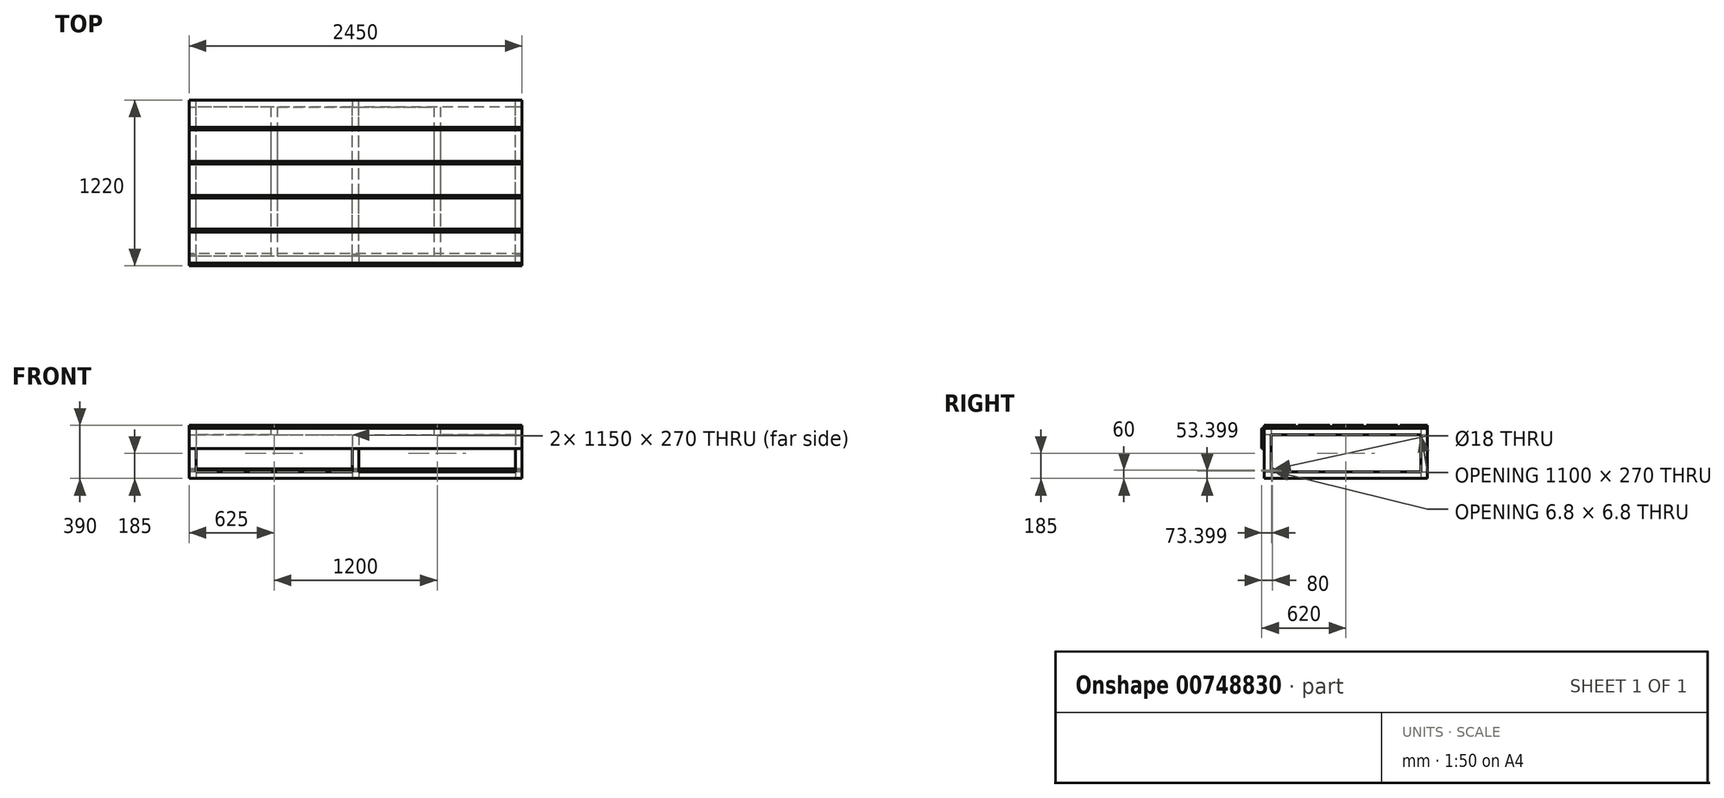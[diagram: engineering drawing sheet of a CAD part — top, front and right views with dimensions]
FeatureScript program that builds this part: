
annotation { "Feature Type Name" : "Feature", "Feature Type Description" : "" }
export const myFeature = defineFeature(function(context is Context, id is Id, definition is map)
    precondition{}
    {
        {
            var Q0;
            Q0=qCreatedBy(makeId("Top.planeOp"),FACE);
            var sketch = newSketch(context, id + "F0", { "sketchPlane" : qUnion([Q0])});
            skLineSegment(sketch, "E0.bottom", {"start": v(1225, -600) * mm, "end": v(-1225, -600) * mm});
            skLineSegment(sketch, "E0.top", {"start": v(1225, 600) * mm, "end": v(-1225, 600) * mm});
            skLineSegment(sketch, "E0.left", {"start": v(1225, -600) * mm, "end": v(1225, 600) * mm});
            skLineSegment(sketch, "E0.right", {"start": v(-1225, -600) * mm, "end": v(-1225, 600) * mm});
            skPoint(sketch, "E0.middle", {"position": v(0, 0) * mm});
            skLineSegment(sketch, "E1.0", {"start": v(1225, 550) * mm, "end": v(-1225, 550) * mm});
            skLineSegment(sketch, "E2.0", {"start": v(1227.5, -600) * mm, "end": v(1227.5, 600) * mm});
            skLineSegment(sketch, "E3.0", {"start": v(1175, -600) * mm, "end": v(1175, 600) * mm});
            skLineSegment(sketch, "E4.0", {"start": v(1225, -550) * mm, "end": v(-1225, -550) * mm});
            skLineSegment(sketch, "E5.0", {"start": v(-1175, -600) * mm, "end": v(-1175, 600) * mm});
            skLineSegment(sketch, "E6", {"start": v(0, 0) * mm, "end": v(0, 550) * mm});
            skLineSegment(sketch, "E7", {"start": v(0, 0) * mm, "end": v(0, -550) * mm});
            skLineSegment(sketch, "E8.0", {"start": v(25, 0) * mm, "end": v(25, 550) * mm});
            skLineSegment(sketch, "E9.0", {"start": v(-25, 0) * mm, "end": v(-25, 550) * mm});
            skLineSegment(sketch, "E10.0", {"start": v(-25, 0) * mm, "end": v(-25, -550) * mm});
            skLineSegment(sketch, "E11.0", {"start": v(25, 0) * mm, "end": v(25, -550) * mm});
            skSolve(sketch);
        }
        {
            var Q0;
            Q0=qSketchRegion(id+"F0",true);
            var Q1;
            {var subQ1=sQuery(id+"F0.wireOp",EDGE,"E6");Q1=makeQuery(id+"F0.imprint","IMPRINT",FACE,{"disambiguationData":[TD([[makeQuery(id+"F0.imprint","IMPRINT",EDGE,{"derivedFrom":subQ1}),-1.0]])]});}
            var Q2;
            {var subQ3=sQuery(id+"F0.wireOp",EDGE,"E6");Q2=makeQuery(id+"F0.imprint","IMPRINT",FACE,{"disambiguationData":[TD([[makeQuery(id+"F0.imprint","IMPRINT",EDGE,{"derivedFrom":subQ3}),1.0]])]});}
            extrude(context, id + "F1", {"entities" : qUnion([Q0, Q1, Q2]), "depth" : 50 * mm, "offsetDistance" : 25 * mm});
        }
        {
            var Q0;
            Q0=makeQuery(id+"F1.opExtrude","CAP_FACE",FACE,{"disambiguationData":[OSD([sQuery(id+"F0.wireOp",EDGE,"E0.bottom"),sQuery(id+"F0.wireOp",EDGE,"E0.top"),sQuery(id+"F0.wireOp",EDGE,"E0.left"),sQuery(id+"F0.wireOp",EDGE,"E0.right"),sQuery(id+"F0.wireOp",EDGE,"E1.0"),sQuery(id+"F0.wireOp",EDGE,"E3.0"),sQuery(id+"F0.wireOp",EDGE,"E4.0"),sQuery(id+"F0.wireOp",EDGE,"E5.0"),sQuery(id+"F0.wireOp",EDGE,"E8.0"),sQuery(id+"F0.wireOp",EDGE,"E9.0"),sQuery(id+"F0.wireOp",EDGE,"E10.0"),sQuery(id+"F0.wireOp",EDGE,"E11.0")])],"isStart":false});
            var sketch = newSketch(context, id + "F2", { "sketchPlane" : qUnion([Q0])});
            skLineSegment(sketch, "E12", {"start": v(-25, 550) * mm, "end": v(25, 550) * mm});
            skLineSegment(sketch, "E13", {"start": v(25, 550) * mm, "end": v(25, 600) * mm});
            skLineSegment(sketch, "E14", {"start": v(25, 600) * mm, "end": v(-25, 600) * mm});
            skLineSegment(sketch, "E15", {"start": v(-25, 600) * mm, "end": v(-25, 550) * mm});
            skLineSegment(sketch, "E16", {"start": v(-1175, 550) * mm, "end": v(-1175, 600) * mm});
            skLineSegment(sketch, "E17", {"start": v(-1175, 600) * mm, "end": v(-1225, 600) * mm});
            skLineSegment(sketch, "E18", {"start": v(-1225, 600) * mm, "end": v(-1225, 550) * mm});
            skLineSegment(sketch, "E19", {"start": v(-1225, 550) * mm, "end": v(-1175, 550) * mm});
            skLineSegment(sketch, "E20", {"start": v(-1175, -550) * mm, "end": v(-1175, -600) * mm});
            skLineSegment(sketch, "E21", {"start": v(-1175, -600) * mm, "end": v(-1225, -600) * mm});
            skLineSegment(sketch, "E22", {"start": v(-1225, -600) * mm, "end": v(-1225, -550) * mm});
            skLineSegment(sketch, "E23", {"start": v(-1225, -550) * mm, "end": v(-1175, -550) * mm});
            skLineSegment(sketch, "E24", {"start": v(-25, -550) * mm, "end": v(25, -550) * mm});
            skLineSegment(sketch, "E25", {"start": v(25, -550) * mm, "end": v(25, -600) * mm});
            skLineSegment(sketch, "E26", {"start": v(25, -600) * mm, "end": v(-25, -600) * mm});
            skPoint(sketch, "E26.endSnap0", {"position": v(0, -600) * mm});
            skLineSegment(sketch, "E27", {"start": v(-25, -600) * mm, "end": v(-25, -550) * mm});
            skLineSegment(sketch, "E28", {"start": v(1175, -550) * mm, "end": v(1225, -550) * mm});
            skLineSegment(sketch, "E29", {"start": v(1225, -550) * mm, "end": v(1225, -600) * mm});
            skLineSegment(sketch, "E30", {"start": v(1225, -600) * mm, "end": v(1175, -600) * mm});
            skLineSegment(sketch, "E31", {"start": v(1175, -600) * mm, "end": v(1175, -550) * mm});
            skLineSegment(sketch, "E32", {"start": v(1175, 550) * mm, "end": v(1175, 600) * mm});
            skLineSegment(sketch, "E33", {"start": v(1175, 600) * mm, "end": v(1225, 600) * mm});
            skLineSegment(sketch, "E34", {"start": v(1225, 600) * mm, "end": v(1225, 550) * mm});
            skLineSegment(sketch, "E35", {"start": v(1225, 550) * mm, "end": v(1175, 550) * mm});
            skSolve(sketch);
        }
        {
            var Q0;
            Q0=qSketchRegion(id+"F2",true);
            extrude(context, id + "F3", {"entities" : qUnion([Q0]), "operationType" : NewBodyOperationType.ADD, "depth" : 270 * mm, "offsetDistance" : 25 * mm});
        }
        {
            var Q0;
            Q0=makeQuery(id+"F3.opExtrude","CAP_FACE",FACE,{"disambiguationData":[OSD([sQuery(id+"F2.wireOp",EDGE,"E12"),sQuery(id+"F2.wireOp",EDGE,"E13"),sQuery(id+"F2.wireOp",EDGE,"E14"),sQuery(id+"F2.wireOp",EDGE,"E15")])],"isStart":false});
            var sketch = newSketch(context, id + "F4", { "sketchPlane" : qUnion([Q0])});
            skLineSegment(sketch, "E36.bottom", {"start": v(-1225, 600) * mm, "end": v(1225, 600) * mm});
            skLineSegment(sketch, "E36.top", {"start": v(-1225, -600) * mm, "end": v(1225, -600) * mm});
            skLineSegment(sketch, "E36.left", {"start": v(-1225, 600) * mm, "end": v(-1225, -600) * mm});
            skLineSegment(sketch, "E36.right", {"start": v(1225, 600) * mm, "end": v(1225, -600) * mm});
            skLineSegment(sketch, "E37.bottom", {"start": v(1175, -550) * mm, "end": v(-1175, -550) * mm});
            skLineSegment(sketch, "E37.top", {"start": v(1175, 550) * mm, "end": v(-1175, 550) * mm});
            skLineSegment(sketch, "E37.left", {"start": v(1175, -550) * mm, "end": v(1175, 550) * mm});
            skLineSegment(sketch, "E37.right", {"start": v(-1175, -550) * mm, "end": v(-1175, 550) * mm});
            skLineSegment(sketch, "E38.bottom", {"start": v(-25, 550) * mm, "end": v(25, 550) * mm});
            skLineSegment(sketch, "E38.top", {"start": v(-25, -550) * mm, "end": v(25, -550) * mm});
            skLineSegment(sketch, "E38.left", {"start": v(-25, 550) * mm, "end": v(-25, -550) * mm});
            skLineSegment(sketch, "E38.right", {"start": v(25, 550) * mm, "end": v(25, -550) * mm});
            skLineSegment(sketch, "E39", {"start": v(-25, 550) * mm, "end": v(-1175, 550) * mm});
            skLineSegment(sketch, "E40", {"start": v(-600, 550) * mm, "end": v(-600, -550) * mm});
            skLineSegment(sketch, "E41.0", {"start": v(-625, 550) * mm, "end": v(-625, -550) * mm});
            skLineSegment(sketch, "E42.0", {"start": v(-575, 550) * mm, "end": v(-575, -550) * mm});
            skLineSegment(sketch, "E43", {"start": v(25, 550) * mm, "end": v(1175, 550) * mm});
            skLineSegment(sketch, "E44", {"start": v(600, 550) * mm, "end": v(600, -550) * mm});
            skLineSegment(sketch, "E45.0", {"start": v(575, 550) * mm, "end": v(575, -550) * mm});
            skLineSegment(sketch, "E46.0", {"start": v(625, 550) * mm, "end": v(625, -550) * mm});
            skSolve(sketch);
        }
        {
            var Q0;
            Q0=qSketchRegion(id+"F4",true);
            var Q1;
            {var subQ0=sQuery(id+"F4.wireOp",EDGE,"E40");Q1=makeQuery(id+"F4.imprint","IMPRINT",FACE,{"disambiguationData":[TD([[makeQuery(id+"F4.imprint","IMPRINT",EDGE,{"derivedFrom":subQ0}),1.0]])]});}
            var Q2;
            {var subQ0=sQuery(id+"F4.wireOp",EDGE,"E40");Q2=makeQuery(id+"F4.imprint","IMPRINT",FACE,{"disambiguationData":[TD([[makeQuery(id+"F4.imprint","IMPRINT",EDGE,{"derivedFrom":subQ0}),-1.0]])]});}
            var Q3;
            {var subQ0=sQuery(id+"F4.wireOp",EDGE,"E44");Q3=makeQuery(id+"F4.imprint","IMPRINT",FACE,{"disambiguationData":[TD([[makeQuery(id+"F4.imprint","IMPRINT",EDGE,{"derivedFrom":subQ0}),1.0]])]});}
            var Q4;
            {var subQ0=sQuery(id+"F4.wireOp",EDGE,"E44");Q4=makeQuery(id+"F4.imprint","IMPRINT",FACE,{"disambiguationData":[TD([[makeQuery(id+"F4.imprint","IMPRINT",EDGE,{"derivedFrom":subQ0}),-1.0]])]});}
            var Q5;
            Q5=makeQuery(id+"F4.imprint","IMPRINT",FACE,{"disambiguationData":[TD([[makeQuery(id+"F4.imprint","IMPRINT",EDGE,{"derivedFrom":sQuery(id+"F4.wireOp",EDGE,"E38.bottom")}),-1.0]])]});
            extrude(context, id + "F5", {"entities" : qUnion([Q0, Q1, Q2, Q3, Q4, Q5]), "operationType" : NewBodyOperationType.ADD, "depth" : 50 * mm, "offsetDistance" : 25 * mm});
        }
        {
            var Q0;
            Q0=makeQuery(id+"F5.boolean.opBoolean","MERGE",FACE,{"derivedFrom":[makeQuery(id+"F3.boolean.opBoolean","MERGE",FACE,{"derivedFrom":[makeQuery(id+"F1.opExtrude","SWEPT_FACE",FACE,{"disambiguationData":[OSD([sQuery(id+"F0.wireOp",EDGE,"E0.right")])]}),makeQuery(id+"F3.opExtrude","SWEPT_FACE",FACE,{"disambiguationData":[OSD([sQuery(id+"F2.wireOp",EDGE,"E18")])]}),makeQuery(id+"F3.opExtrude","SWEPT_FACE",FACE,{"disambiguationData":[OSD([sQuery(id+"F2.wireOp",EDGE,"E22")])]})]}),makeQuery(id+"F5.opExtrude","SWEPT_FACE",FACE,{"disambiguationData":[OSD([sQuery(id+"F4.wireOp",EDGE,"E36.left")])]})]});
            var sketch = newSketch(context, id + "F6", { "sketchPlane" : qUnion([Q0])});
            skLineSegment(sketch, "E47", {"start": v(550, 50) * mm, "end": v(550, 60) * mm});
            skLineSegment(sketch, "E48", {"start": v(550, 60) * mm, "end": v(540, 60) * mm});
            skCircle(sketch, "E49", {"center": v(540, 60) * mm, "radius": 10.5 * mm});
            skCircle(sketch, "E50", {"center": v(540, 60) * mm, "radius": 9 * mm});
            skSolve(sketch);
        }
        {
            var Q0;
            Q0=qSketchRegion(id+"F6",true);
            extrude(context, id + "F7", {"entities" : qUnion([Q0]), "operationType" : NewBodyOperationType.ADD, "oppositeDirection" : true, "depth" : 2450 * mm, "offsetDistance" : 25 * mm});
        }
        {
            var Q0;
            Q0=makeQuery(id+"F5.boolean.opBoolean","MERGE",FACE,{"derivedFrom":[makeQuery(id+"F3.boolean.opBoolean","MERGE",FACE,{"derivedFrom":[makeQuery(id+"F1.opExtrude","SWEPT_FACE",FACE,{"disambiguationData":[OSD([sQuery(id+"F0.wireOp",EDGE,"E0.bottom")])]}),makeQuery(id+"F3.opExtrude","SWEPT_FACE",FACE,{"disambiguationData":[OSD([sQuery(id+"F2.wireOp",EDGE,"E21")])]}),makeQuery(id+"F3.opExtrude","SWEPT_FACE",FACE,{"disambiguationData":[OSD([sQuery(id+"F2.wireOp",EDGE,"E26")])]}),makeQuery(id+"F3.opExtrude","SWEPT_FACE",FACE,{"disambiguationData":[OSD([sQuery(id+"F2.wireOp",EDGE,"E30")])]})]}),makeQuery(id+"F5.opExtrude","SWEPT_FACE",FACE,{"disambiguationData":[OSD([sQuery(id+"F4.wireOp",EDGE,"E36.top")])]})]});
            var sketch = newSketch(context, id + "F8", { "sketchPlane" : qUnion([Q0])});
            skLineSegment(sketch, "E51.bottom", {"start": v(1225, 370) * mm, "end": v(-1275, 370) * mm});
            skLineSegment(sketch, "E51.top", {"start": v(1225, 220) * mm, "end": v(-1275, 220) * mm});
            skLineSegment(sketch, "E51.left", {"start": v(1225, 370) * mm, "end": v(1225, 220) * mm});
            skLineSegment(sketch, "E51.right", {"start": v(-1275, 370) * mm, "end": v(-1275, 220) * mm});
            skLineSegment(sketch, "E52", {"start": v(-1225, 370) * mm, "end": v(-1275, 370) * mm});
            skSolve(sketch);
        }
        {
            var Q0;
            Q0=qSketchRegion(id+"F8",true);
            extrude(context, id + "F9", {"entities" : qUnion([Q0]), "depth" : 20 * mm, "offsetDistance" : 25 * mm});
        }
        {
            var Q0;
            Q0=makeQuery(id+"F5.opExtrude","CAP_FACE",FACE,{"disambiguationData":[OSD([sQuery(id+"F4.wireOp",EDGE,"E36.bottom"),sQuery(id+"F4.wireOp",EDGE,"E36.top"),sQuery(id+"F4.wireOp",EDGE,"E36.left"),sQuery(id+"F4.wireOp",EDGE,"E36.right"),sQuery(id+"F4.wireOp",EDGE,"E37.bottom"),sQuery(id+"F4.wireOp",EDGE,"E37.left"),sQuery(id+"F4.wireOp",EDGE,"E37.right"),sQuery(id+"F4.wireOp",EDGE,"E38.left"),sQuery(id+"F4.wireOp",EDGE,"E38.right"),sQuery(id+"F4.wireOp",EDGE,"E39"),sQuery(id+"F4.wireOp",EDGE,"E41.0"),sQuery(id+"F4.wireOp",EDGE,"E42.0"),sQuery(id+"F4.wireOp",EDGE,"E43"),sQuery(id+"F4.wireOp",EDGE,"E45.0"),sQuery(id+"F4.wireOp",EDGE,"E46.0")])],"isStart":false});
            var sketch = newSketch(context, id + "F10", { "sketchPlane" : qUnion([Q0])});
            skLineSegment(sketch, "E53.bottom", {"start": v(1225, 600) * mm, "end": v(-1275, 600) * mm});
            skLineSegment(sketch, "E53.top", {"start": v(1225, -600) * mm, "end": v(-1275, -600) * mm});
            skLineSegment(sketch, "E53.left", {"start": v(1225, 600) * mm, "end": v(1225, -600) * mm});
            skLineSegment(sketch, "E53.right", {"start": v(-1275, 600) * mm, "end": v(-1275, -600) * mm});
            skSolve(sketch);
        }
        {
            var Q0;
            Q0=qSketchRegion(id+"F10",true);
            extrude(context, id + "F11", {"entities" : qUnion([Q0]), "depth" : 20 * mm, "offsetDistance" : 25 * mm});
        }
        {
            var Q0;
            Q0=makeQuery(id+"F11.opExtrude","SWEPT_FACE",FACE,{"disambiguationData":[OSD([sQuery(id+"F10.wireOp",EDGE,"E53.right")])]});
            var sketch = newSketch(context, id + "F12", { "sketchPlane" : qUnion([Q0])});
            skLineSegment(sketch, "E54", {"start": v(620, 370) * mm, "end": v(600, 370) * mm});
            skLineSegment(sketch, "E55", {"start": v(600, 370) * mm, "end": v(600, 390) * mm});
            skLineSegment(sketch, "E56", {"start": v(600, 390) * mm, "end": v(620, 390) * mm});
            skLineSegment(sketch, "E57", {"start": v(620, 390) * mm, "end": v(620, 370) * mm});
            skLineSegment(sketch, "E58.1.0.0", {"start": v(370, 390) * mm, "end": v(370, 370) * mm});
            skLineSegment(sketch, "E58.1.0.1", {"start": v(350, 390) * mm, "end": v(370, 390) * mm});
            skLineSegment(sketch, "E58.1.0.2", {"start": v(350, 370) * mm, "end": v(350, 390) * mm});
            skLineSegment(sketch, "E58.1.0.3", {"start": v(370, 370) * mm, "end": v(350, 370) * mm});
            skLineSegment(sketch, "E58.2.0.0", {"start": v(120, 390) * mm, "end": v(120, 370) * mm});
            skLineSegment(sketch, "E58.2.0.1", {"start": v(100, 390) * mm, "end": v(120, 390) * mm});
            skLineSegment(sketch, "E58.2.0.2", {"start": v(100, 370) * mm, "end": v(100, 390) * mm});
            skLineSegment(sketch, "E58.2.0.3", {"start": v(120, 370) * mm, "end": v(100, 370) * mm});
            skLineSegment(sketch, "E58.3.0.0", {"start": v(-130, 390) * mm, "end": v(-130, 370) * mm});
            skLineSegment(sketch, "E58.3.0.1", {"start": v(-150, 390) * mm, "end": v(-130, 390) * mm});
            skLineSegment(sketch, "E58.3.0.2", {"start": v(-150, 370) * mm, "end": v(-150, 390) * mm});
            skLineSegment(sketch, "E58.3.0.3", {"start": v(-130, 370) * mm, "end": v(-150, 370) * mm});
            skLineSegment(sketch, "E58.4.0.0", {"start": v(-380, 390) * mm, "end": v(-380, 370) * mm});
            skLineSegment(sketch, "E58.4.0.1", {"start": v(-400, 390) * mm, "end": v(-380, 390) * mm});
            skLineSegment(sketch, "E58.4.0.2", {"start": v(-400, 370) * mm, "end": v(-400, 390) * mm});
            skLineSegment(sketch, "E58.4.0.3", {"start": v(-380, 370) * mm, "end": v(-400, 370) * mm});
            skLineSegment(sketch, "E58.direction1", {"start": v(620, 370) * mm, "end": v(370, 370) * mm, "construction": true});
            skSolve(sketch);
        }
        {
            var Q0;
            Q0=makeQuery(id+"F12.imprint","IMPRINT",FACE,{"disambiguationData":[TD([[makeQuery(id+"F12.imprint","IMPRINT",EDGE,{"derivedFrom":sQuery(id+"F12.wireOp",EDGE,"E54")}),-1.0]])]});
            var Q1;
            Q1=makeQuery(id+"F12.imprint","IMPRINT",FACE,{"disambiguationData":[TD([[makeQuery(id+"F12.imprint","IMPRINT",EDGE,{"derivedFrom":sQuery(id+"F12.wireOp",EDGE,"E58.1.0.0")}),-1.0]])]});
            var Q2;
            Q2=makeQuery(id+"F12.imprint","IMPRINT",FACE,{"disambiguationData":[TD([[makeQuery(id+"F12.imprint","IMPRINT",EDGE,{"derivedFrom":sQuery(id+"F12.wireOp",EDGE,"E58.2.0.0")}),-1.0]])]});
            var Q3;
            Q3=makeQuery(id+"F12.imprint","IMPRINT",FACE,{"disambiguationData":[TD([[makeQuery(id+"F12.imprint","IMPRINT",EDGE,{"derivedFrom":sQuery(id+"F12.wireOp",EDGE,"E58.3.0.0")}),-1.0]])]});
            var Q4;
            Q4=makeQuery(id+"F12.imprint","IMPRINT",FACE,{"disambiguationData":[TD([[makeQuery(id+"F12.imprint","IMPRINT",EDGE,{"derivedFrom":sQuery(id+"F12.wireOp",EDGE,"E58.4.0.0")}),-1.0]])]});
            var Q5;
            Q5=makeQuery(id+"F11.opExtrude","SWEPT_FACE",FACE,{"disambiguationData":[OSD([sQuery(id+"F10.wireOp",EDGE,"E53.left")])]});
            extrude(context, id + "F13", {"entities" : qUnion([Q0, Q1, Q2, Q3, Q4]), "operationType" : NewBodyOperationType.REMOVE, "endBound" : BoundingType.UP_TO_SURFACE, "oppositeDirection" : true, "depth" : 25 * mm, "endBoundEntityFace" : qUnion([Q5]), "offsetDistance" : 25 * mm});
        }
        {
            var Q0;
            Q0=makeQuery(id+"F9.opExtrude","CAP_FACE",FACE,{"disambiguationData":[OSD([sQuery(id+"F8.wireOp",EDGE,"E51.bottom"),sQuery(id+"F8.wireOp",EDGE,"E51.top"),sQuery(id+"F8.wireOp",EDGE,"E51.left"),sQuery(id+"F8.wireOp",EDGE,"E51.right"),sQuery(id+"F8.wireOp",EDGE,"E52")])],"isStart":false});
            var sketch = newSketch(context, id + "F14", { "sketchPlane" : qUnion([Q0])});
            skLineSegment(sketch, "E59.bottom", {"start": v(-1225, 220) * mm, "end": v(-1275, 220) * mm});
            skLineSegment(sketch, "E59.top", {"start": v(-1225, 390) * mm, "end": v(-1275, 390) * mm});
            skLineSegment(sketch, "E59.left", {"start": v(-1225, 220) * mm, "end": v(-1225, 390) * mm});
            skLineSegment(sketch, "E59.right", {"start": v(-1275, 220) * mm, "end": v(-1275, 390) * mm});
            skSolve(sketch);
        }
        {
            var Q0;
            Q0 = qSketchRegion(id + "F14", true);
            var Q1;
            Q1=makeQuery(id+"F11.opExtrude","SWEPT_FACE",FACE,{"disambiguationData":[OSD([sQuery(id+"F10.wireOp",EDGE,"E53.bottom")])]});
            extrude(context, id + "F15", {"entities" : qUnion([Q0]), "endBound" : BoundingType.UP_TO_SURFACE, "oppositeDirection" : true, "depth" : 275.72 * mm, "endBoundEntityFace" : qUnion([Q1]), "offsetDistance" : 25 * mm});
        }
        {
            var Q0;
            Q0=makeQuery(id+"F15.opExtrude","SWEPT_BODY",BODY,{"disambiguationData":[OSD([sQuery(id+"F14.wireOp",EDGE,"E59.bottom"),sQuery(id+"F14.wireOp",EDGE,"E59.top"),sQuery(id+"F14.wireOp",EDGE,"E59.left"),sQuery(id+"F14.wireOp",EDGE,"E59.right")])]});
            var Q1;
            Q1=makeQuery(id+"F9.opExtrude","SWEPT_BODY",BODY,{"disambiguationData":[OSD([sQuery(id+"F8.wireOp",EDGE,"E51.bottom"),sQuery(id+"F8.wireOp",EDGE,"E51.top"),sQuery(id+"F8.wireOp",EDGE,"E51.left"),sQuery(id+"F8.wireOp",EDGE,"E51.right"),sQuery(id+"F8.wireOp",EDGE,"E52")])]});
            var Q2;
            Q2=makeQuery(id+"F13.boolean.opBoolean","SPLIT",BODY,{"disambiguationData":[OD(1.0)],"derivedFrom":makeQuery(id+"F11.opExtrude","SWEPT_BODY",BODY,{"disambiguationData":[OSD([sQuery(id+"F10.wireOp",EDGE,"E53.bottom"),sQuery(id+"F10.wireOp",EDGE,"E53.top"),sQuery(id+"F10.wireOp",EDGE,"E53.left"),sQuery(id+"F10.wireOp",EDGE,"E53.right")])]})});
            var Q3;
            Q3=makeQuery(id+"F13.boolean.opBoolean","SPLIT",BODY,{"disambiguationData":[OD(2.0)],"derivedFrom":makeQuery(id+"F11.opExtrude","SWEPT_BODY",BODY,{"disambiguationData":[OSD([sQuery(id+"F10.wireOp",EDGE,"E53.bottom"),sQuery(id+"F10.wireOp",EDGE,"E53.top"),sQuery(id+"F10.wireOp",EDGE,"E53.left"),sQuery(id+"F10.wireOp",EDGE,"E53.right")])]})});
            var Q4;
            Q4=makeQuery(id+"F13.boolean.opBoolean","SPLIT",BODY,{"disambiguationData":[OD(3.0)],"derivedFrom":makeQuery(id+"F11.opExtrude","SWEPT_BODY",BODY,{"disambiguationData":[OSD([sQuery(id+"F10.wireOp",EDGE,"E53.bottom"),sQuery(id+"F10.wireOp",EDGE,"E53.top"),sQuery(id+"F10.wireOp",EDGE,"E53.left"),sQuery(id+"F10.wireOp",EDGE,"E53.right")])]})});
            var Q5;
            Q5=makeQuery(id+"F13.boolean.opBoolean","SPLIT",BODY,{"disambiguationData":[OD(4.0)],"derivedFrom":makeQuery(id+"F11.opExtrude","SWEPT_BODY",BODY,{"disambiguationData":[OSD([sQuery(id+"F10.wireOp",EDGE,"E53.bottom"),sQuery(id+"F10.wireOp",EDGE,"E53.top"),sQuery(id+"F10.wireOp",EDGE,"E53.left"),sQuery(id+"F10.wireOp",EDGE,"E53.right")])]})});
            var Q6;
            Q6=makeQuery(id+"F13.boolean.opBoolean","SPLIT",BODY,{"disambiguationData":[OD(0.0)],"derivedFrom":makeQuery(id+"F11.opExtrude","SWEPT_BODY",BODY,{"disambiguationData":[OSD([sQuery(id+"F10.wireOp",EDGE,"E53.bottom"),sQuery(id+"F10.wireOp",EDGE,"E53.top"),sQuery(id+"F10.wireOp",EDGE,"E53.left"),sQuery(id+"F10.wireOp",EDGE,"E53.right")])]})});
            booleanBodies(context, id + "F16", {"operationType" : BooleanOperationType.SUBTRACTION, "tools" : qUnion([Q0]), "targets" : qUnion([Q1, Q2, Q3, Q4, Q5, Q6])});
        }
    });
